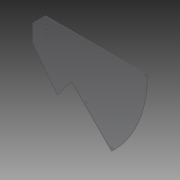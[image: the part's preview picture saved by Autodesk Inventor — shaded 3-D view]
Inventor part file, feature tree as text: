
AUTODESK INVENTOR PART (.ipt)
format: ipt  version: 2014 SP1 (Build 180222100, 222)  size: 100,352 bytes
history: native  units: in
note: dims shown in document units (in); Inventor stores cm internally (conversion verified against a paired STEP export)
features: reference x2, extrude x1, sketch x1
ambient origin geometry x8: Origin, YZ Plane, XZ Plane, XY Plane, X Axis, Y Axis, Z Axis, Center Point
bodies: Solid1 (feature_tree)
feature tree (4):
  extrude  "Extrusion1"  [1 undecoded]
  sketch  "Sketch1"  dims[d0=0.0312in d1=0.0in]
  reference  "Reference1"
  reference  "Reference2"
note: 1 required parameter value undecoded (feature->parameter linkage not recoverable at this tier; creation-order binding heuristic only, values carry confidence <= 0.55)
